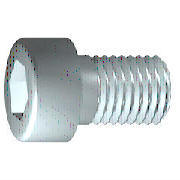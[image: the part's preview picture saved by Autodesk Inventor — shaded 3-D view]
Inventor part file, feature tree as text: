
AUTODESK INVENTOR PART (.ipt)
format: ipt  version: 2024.3 (Build 283343000, 343)  size: 186,880 bytes
history: native  units: mm (DEFAULTED — no unit token found)
features: extrude x1, plane x1, fillet x1
ambient origin geometry x7: Origin, YZ Plane, XY Plane, X Axis, Y Axis, Z Axis, Center Point
bodies: Solid1 (feature_tree), Body (feature_tree)
feature tree (3):
  extrude  "Slot"  Depth=20.0mm
  plane  "Work Plane1"
  fillet  "Fillet2"  Radius=0.429515mm
